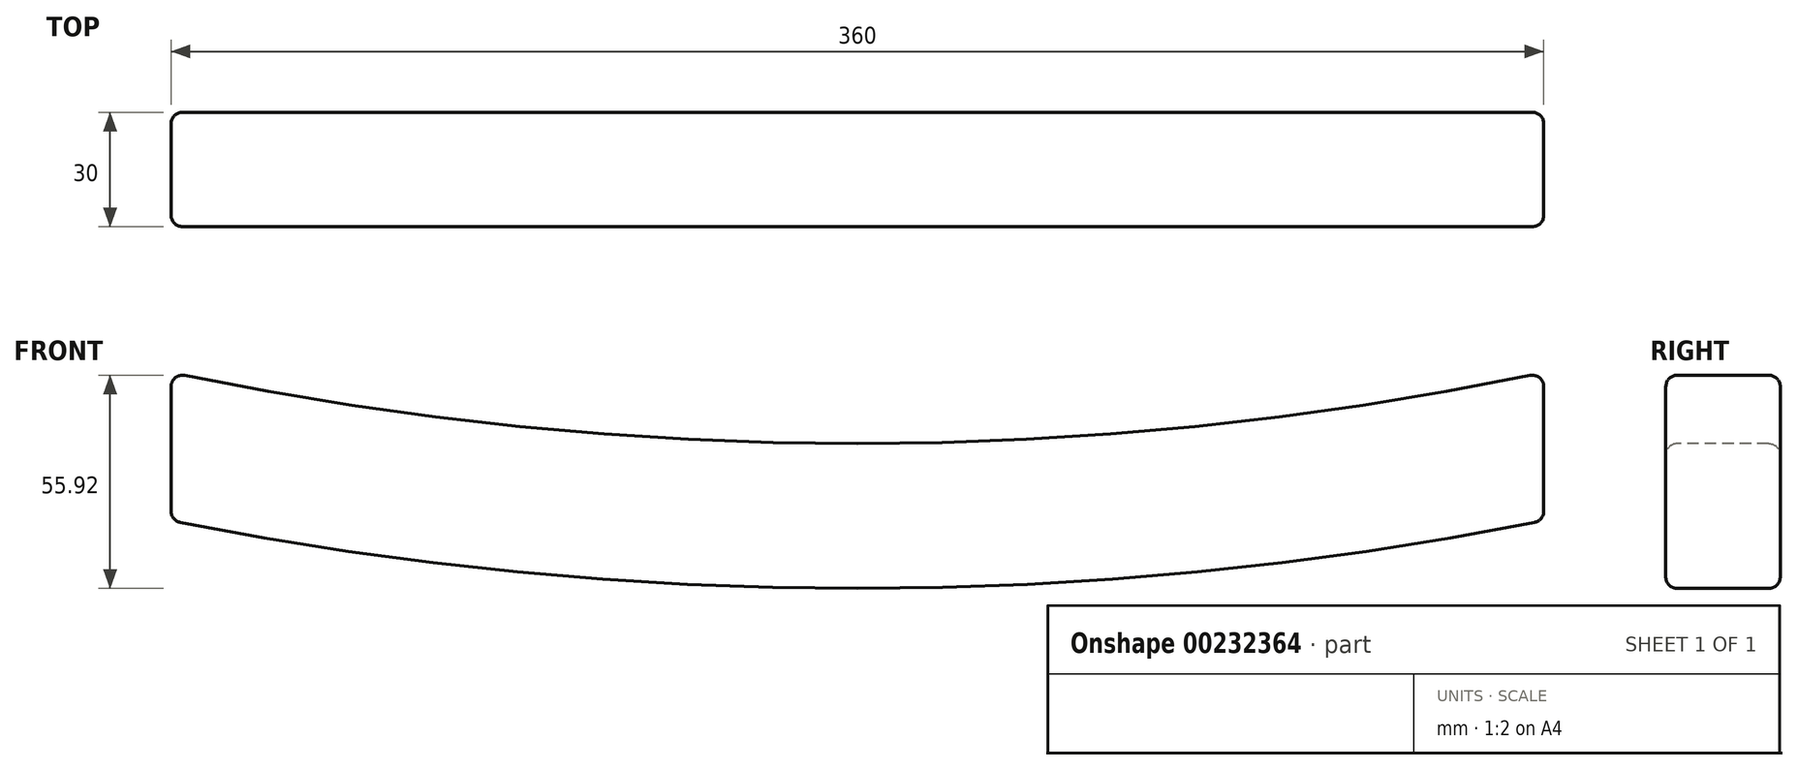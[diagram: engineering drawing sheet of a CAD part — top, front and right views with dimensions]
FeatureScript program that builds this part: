
annotation { "Feature Type Name" : "Feature", "Feature Type Description" : "" }
export const myFeature = defineFeature(function(context is Context, id is Id, definition is map)
    precondition{}
    {
        {
            var Q0;
            Q0=qCreatedBy(makeId("Front.planeOp"),FACE);
            var sketch = newSketch(context, id + "F0", { "sketchPlane" : qUnion([Q0])});
            skLineSegment(sketch, "E0.left", {"start": v(-180, -20.18) * mm, "end": v(-180, -58.97) * mm});
            skLineSegment(sketch, "E0.right", {"start": v(180, -20.18) * mm, "end": v(180, -58.97) * mm});
            skArc(sketch, "E1", {"start": v(-180, -20.18) * mm, "mid": v(0, -38.79) * mm, "end": v(180, -20.18) * mm});
            skArc(sketch, "E2.0", {"start": v(-180, -58.97) * mm, "mid": v(0.14, -76.79) * mm, "end": v(180.27, -58.91) * mm});
            skSolve(sketch);
        }
        {
            var Q0;
            Q0 = qSketchRegion(id + "F0", true);
            extrude(context, id + "F1", {"entities" : qUnion([Q0]), "oppositeDirection" : true, "depth" : 30 * mm});
        }
        {
            var Q0;
            Q0=makeQuery(id+"F1.opExtrude","SWEPT_FACE",FACE,{"disambiguationData":[OSD([sQuery(id+"F0.wireOp",EDGE,"E0.left")])]});
            var Q1;
            Q1=makeQuery(id+"F1.opExtrude","SWEPT_FACE",FACE,{"disambiguationData":[OSD([sQuery(id+"F0.wireOp",EDGE,"E0.right")])]});
            var Q2;
            Q2=makeQuery(id+"F1.opExtrude","CAP_EDGE",EDGE,{"disambiguationData":[OSD([sQuery(id+"F0.wireOp",EDGE,"E1")])],"isStart":true});
            var Q3;
            Q3=makeQuery(id+"F1.opExtrude","CAP_EDGE",EDGE,{"disambiguationData":[OSD([sQuery(id+"F0.wireOp",EDGE,"E1")])],"isStart":false});
            var Q4;
            Q4=makeQuery(id+"F1.opExtrude","CAP_EDGE",EDGE,{"disambiguationData":[OSD([sQuery(id+"F0.wireOp",EDGE,"E2.0")])],"isStart":true});
            var Q5;
            Q5=makeQuery(id+"F1.opExtrude","CAP_EDGE",EDGE,{"disambiguationData":[OSD([sQuery(id+"F0.wireOp",EDGE,"E2.0")])],"isStart":false});
            fillet(context, id + "F2", {"entities" : qUnion([Q0, Q1, Q2, Q3, Q4, Q5]), "radius" : 3 * mm, "tangentPropagation" : true, "allowEdgeOverflow" : false});
        }
    });
